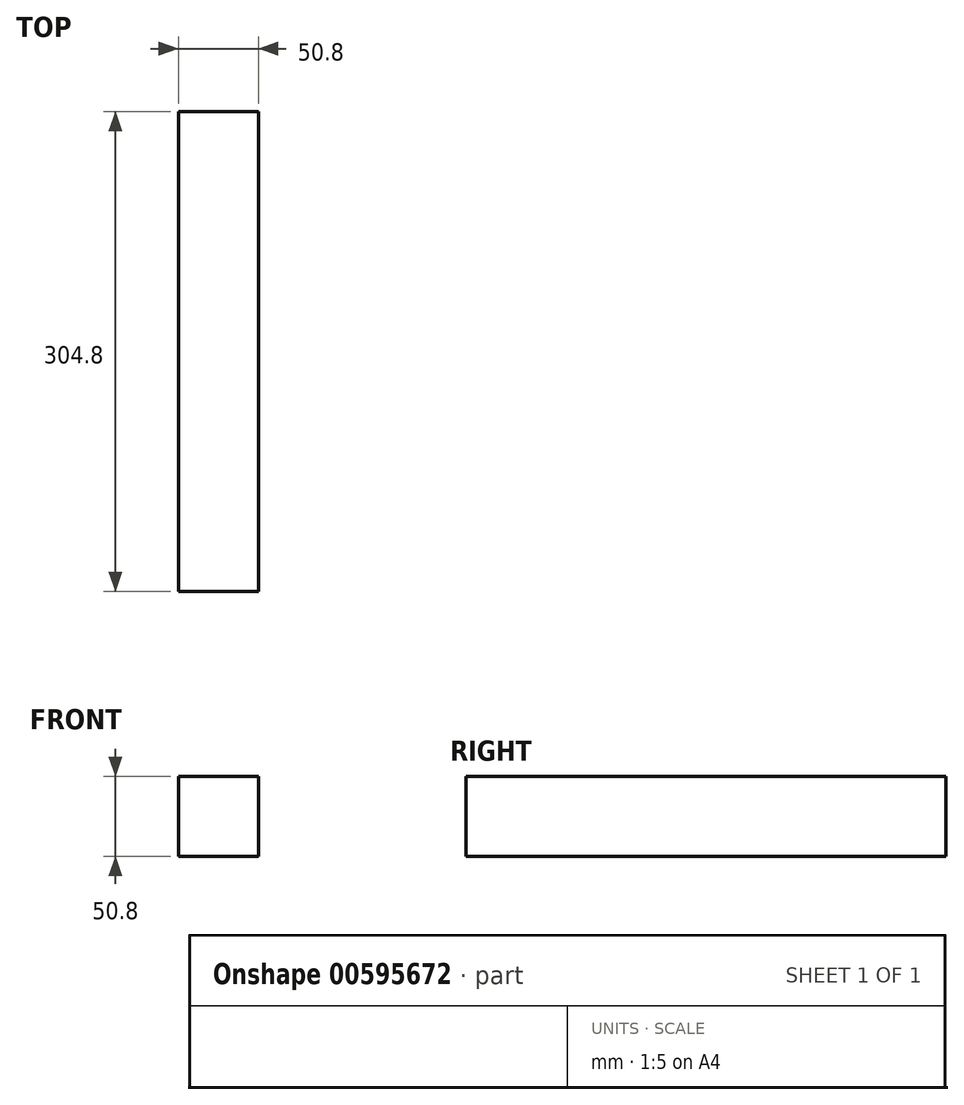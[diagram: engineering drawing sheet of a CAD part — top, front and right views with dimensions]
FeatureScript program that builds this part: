
annotation { "Feature Type Name" : "Feature", "Feature Type Description" : "" }
export const myFeature = defineFeature(function(context is Context, id is Id, definition is map)
    precondition{}
    {
        {
            var Q0;
            Q0=qCreatedBy(makeId("Front.planeOp"),FACE);
            var sketch = newSketch(context, id + "F0", { "sketchPlane" : qUnion([Q0])});
            skLineSegment(sketch, "E0.bottom", {"start": v(-25.4, 25.4) * mm, "end": v(25.4, 25.4) * mm});
            skLineSegment(sketch, "E0.top", {"start": v(-25.4, -25.4) * mm, "end": v(25.4, -25.4) * mm});
            skLineSegment(sketch, "E0.left", {"start": v(-25.4, 25.4) * mm, "end": v(-25.4, -25.4) * mm});
            skLineSegment(sketch, "E0.right", {"start": v(25.4, 25.4) * mm, "end": v(25.4, -25.4) * mm});
            skSolve(sketch);
        }
        {
            var Q0;
            Q0=makeQuery(id+"F0.imprint","IMPRINT",FACE,{"disambiguationData":[TD([[makeQuery(id+"F0.imprint","IMPRINT",EDGE,{"derivedFrom":sQuery(id+"F0.wireOp",EDGE,"E0.bottom")}),-1.0]])]});
            extrude(context, id + "F1", {"entities" : qUnion([Q0]), "depth" : 304.8 * mm, "offsetDistance" : 25.4 * mm});
        }
    });
